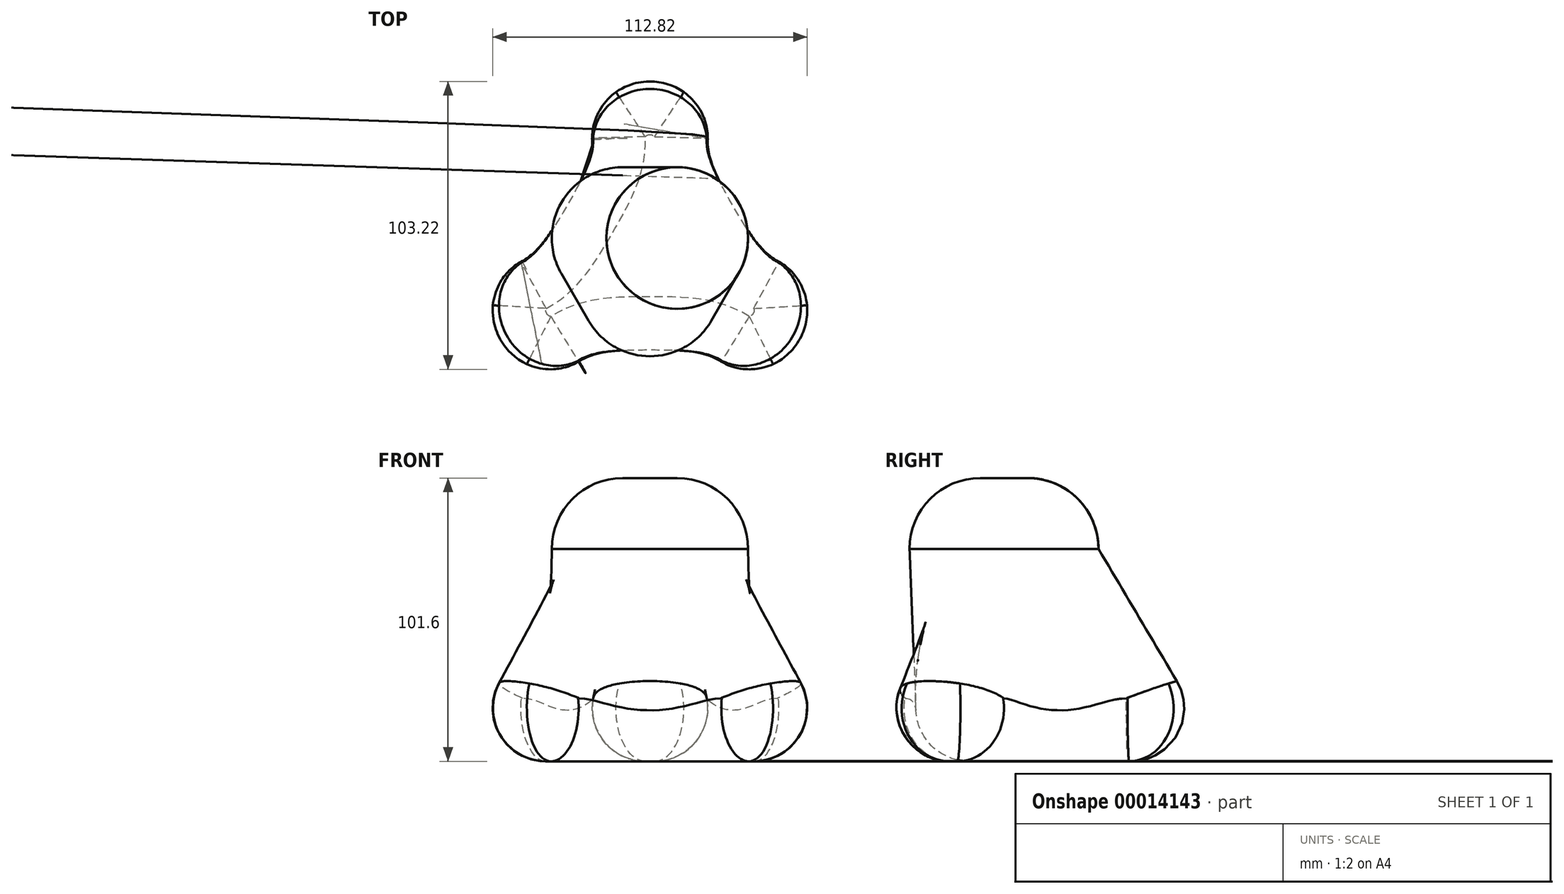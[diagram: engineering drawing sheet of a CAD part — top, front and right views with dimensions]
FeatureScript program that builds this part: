
annotation { "Feature Type Name" : "Feature", "Feature Type Description" : "" }
export const myFeature = defineFeature(function(context is Context, id is Id, definition is map)
    precondition{}
    {
        {
            var Q0;
            Q0=qCreatedBy(makeId("Top.planeOp"),FACE);
            var sketch = newSketch(context, id + "F0", { "sketchPlane" : qUnion([Q0])});
            skArc(sketch, "E0", {"start": v(24.8, 45.28) * mm, "mid": v(0, 76.2) * mm, "end": v(-24.8, 45.28) * mm});
            skArc(sketch, "E1.1.0", {"start": v(-51.6, -1.17) * mm, "mid": v(-66, -38.1) * mm, "end": v(-26.82, -44.11) * mm});
            skArc(sketch, "E1.2.0", {"start": v(26.82, -44.11) * mm, "mid": v(66, -38.1) * mm, "end": v(51.6, -1.17) * mm});
            skPoint(sketch, "E1.center", {"position": v(0, 0) * mm});
            skArc(sketch, "E2", {"start": v(24.8, 45.28) * mm, "mid": v(29.16, 16.83) * mm, "end": v(51.6, -1.17) * mm});
            skArc(sketch, "E3", {"start": v(26.82, -44.11) * mm, "mid": v(0, -33.67) * mm, "end": v(-26.82, -44.11) * mm});
            skArc(sketch, "E4", {"start": v(-51.6, -1.17) * mm, "mid": v(-29.16, 16.83) * mm, "end": v(-24.8, 45.28) * mm});
            skSolve(sketch);
        }
        {
            var Q0;
            Q0=qCreatedBy(makeId("Top.planeOp"),FACE);
            cPlane(context, id + "F1", {"entities" : qUnion([Q0]), "cplaneType" : CPlaneType.OFFSET, "offset" : 76.2 * mm, "width" : 152.4 * mm, "height" : 152.4 * mm});
        }
        {
            var Q0;
            Q0=qCreatedBy(id+"F1.planeOp",FACE);
            var sketch = newSketch(context, id + "F2", { "sketchPlane" : qUnion([Q0])});
            skLineSegment(sketch, "E5.0", {"start": v(-9.8, 31.06) * mm, "end": v(9.8, 31.06) * mm});
            skLineSegment(sketch, "E5.1", {"start": v(31.8, -7.04) * mm, "end": v(22, -24.01) * mm});
            skLineSegment(sketch, "E5.2", {"start": v(-22, -24.01) * mm, "end": v(-31.8, -7.04) * mm});
            skPoint(sketch, "E5.0.midPoint", {"position": v(0, 31.06) * mm});
            skPoint(sketch, "E6.visualSharp", {"position": v(-53.8, 31.06) * mm});
            skArc(sketch, "E6.filletArc", {"start": v(-9.8, 31.06) * mm, "mid": v(-31.8, 18.36) * mm, "end": v(-31.8, -7.04) * mm});
            skPoint(sketch, "E7.visualSharp", {"position": v(53.8, 31.06) * mm});
            skArc(sketch, "E7.filletArc", {"start": v(31.8, -7.04) * mm, "mid": v(31.8, 18.36) * mm, "end": v(9.8, 31.06) * mm});
            skPoint(sketch, "E8.visualSharp", {"position": v(0, -62.11) * mm});
            skArc(sketch, "E8.filletArc", {"start": v(-22, -24.01) * mm, "mid": v(0, -36.71) * mm, "end": v(22, -24.01) * mm});
            skSolve(sketch);
        }
        {
            var Q0;
            Q0=makeQuery(id+"F2.imprint","IMPRINT",FACE,{"disambiguationData":[TD([[makeQuery(id+"F2.imprint","IMPRINT",EDGE,{"derivedFrom":sQuery(id+"F2.wireOp",EDGE,"E5.0")}),-1.0]])]});
            var Q1;
            Q1=makeQuery(id+"F0.imprint","IMPRINT",FACE,{"disambiguationData":[TD([[makeQuery(id+"F0.imprint","IMPRINT",EDGE,{"derivedFrom":sQuery(id+"F0.wireOp",EDGE,"E0")}),1.0]])]});
            loft(context, id + "F3", {"sheetProfilesArray" : [{ "sheetProfileEntities" : qUnion([Q0]) }, { "sheetProfileEntities" : qUnion([Q1]) }]});
        }
        {
            var Q0;
            Q0=makeQuery(id+"F3.opLoft","MID_CAP_EDGE",EDGE,{"disambiguationData":[OSD([sQuery(id+"F0.wireOp",EDGE,"E0"),sQuery(id+"F0.wireOp",EDGE,"E1.1.0"),sQuery(id+"F0.wireOp",EDGE,"E4")])],"capPos":1.0});
            var Q1;
            Q1=makeQuery(id+"F3.opLoft","CAP_FACE",FACE,{"disambiguationData":[OSD([makeQuery(id+"F0.imprint","IMPRINT",FACE,{"disambiguationData":[TD([[makeQuery(id+"F0.imprint","IMPRINT",EDGE,{"derivedFrom":sQuery(id+"F0.wireOp",EDGE,"E0")}),1.0]])]})])],"isStart":true});
            var Q2;
            Q2=makeQuery(id+"F3.opLoft","MID_CAP_EDGE",EDGE,{"disambiguationData":[OSD([sQuery(id+"F0.wireOp",EDGE,"E1.1.0"),sQuery(id+"F0.wireOp",EDGE,"E3"),sQuery(id+"F0.wireOp",EDGE,"E4")])],"capPos":1.0});
            var Q3;
            Q3=makeQuery(id+"F3.opLoft","MID_CAP_EDGE",EDGE,{"disambiguationData":[OSD([sQuery(id+"F0.wireOp",EDGE,"E1.1.0"),sQuery(id+"F0.wireOp",EDGE,"E1.2.0"),sQuery(id+"F0.wireOp",EDGE,"E3")])],"capPos":1.0});
            var Q4;
            Q4=makeQuery(id+"F3.opLoft","MID_CAP_EDGE",EDGE,{"disambiguationData":[OSD([sQuery(id+"F0.wireOp",EDGE,"E1.2.0"),sQuery(id+"F0.wireOp",EDGE,"E2"),sQuery(id+"F0.wireOp",EDGE,"E3")])],"capPos":1.0});
            var Q5;
            Q5=makeQuery(id+"F3.opLoft","MID_CAP_EDGE",EDGE,{"disambiguationData":[OSD([sQuery(id+"F0.wireOp",EDGE,"E0"),sQuery(id+"F0.wireOp",EDGE,"E1.2.0"),sQuery(id+"F0.wireOp",EDGE,"E2")])],"capPos":1.0});
            var Q6;
            Q6=makeQuery(id+"F3.opLoft","MID_CAP_EDGE",EDGE,{"disambiguationData":[OSD([sQuery(id+"F0.wireOp",EDGE,"E0"),sQuery(id+"F0.wireOp",EDGE,"E2"),sQuery(id+"F0.wireOp",EDGE,"E4")])],"capPos":1.0});
            fillet(context, id + "F4", {"entities" : qUnion([Q0, Q1, Q2, Q3, Q4, Q5, Q6]), "radius" : 19.05 * mm, "tangentPropagation" : true, "allowEdgeOverflow" : false});
        }
        {
            var Q0;
            Q0=makeQuery(id+"F3.opLoft","CAP_FACE",FACE,{"disambiguationData":[OSD([makeQuery(id+"F2.imprint","IMPRINT",FACE,{"disambiguationData":[TD([[makeQuery(id+"F2.imprint","IMPRINT",EDGE,{"derivedFrom":sQuery(id+"F2.wireOp",EDGE,"E5.0")}),-1.0]])]})])],"isStart":true});
            extrude(context, id + "F5", {"entities" : qUnion([Q0]), "operationType" : NewBodyOperationType.ADD, "depth" : 25.4 * mm});
        }
        {
            var Q0;
            Q0=makeQuery(id+"F5.opExtrude","CAP_EDGE",EDGE,{"disambiguationData":[OSD([sQuery(id+"F2.wireOp",EDGE,"E5.1"),sQuery(id+"F2.wireOp",EDGE,"E5.2"),sQuery(id+"F2.wireOp",EDGE,"E8.filletArc")])],"isStart":false});
            fillet(context, id + "F6", {"entities" : qUnion([Q0]), "radius" : 25.4 * mm, "tangentPropagation" : true, "allowEdgeOverflow" : false});
        }
    });
